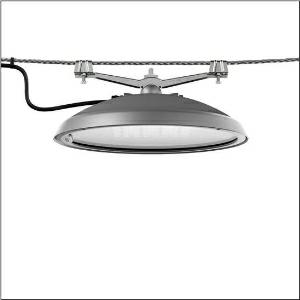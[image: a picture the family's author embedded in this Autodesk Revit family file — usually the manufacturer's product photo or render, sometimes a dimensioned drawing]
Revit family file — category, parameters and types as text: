
# Revit family: dl_50_iq_mini___st1_0s_5xa248w31f08he_4c20
name_source: partatom
category: Lighting Fixtures
units: mm (PartAtom-declared; Revit-internal decimal feet)

## family parameters
Cut with Voids When Loaded = No
Host = Face
Light Source = No
Part Type = Normal
Room Calculation Point = No
Round Connector Dimension = Use Diameter
Shared = No

## types (1)
- --- (1 x LED, 9400 lm, 68.6 W, 3000K)
    Apparent Load = 69 VA
    CIE Flux Codes = 37 72 97 100 100
    Color Rendering = 70
    Color Temperature = 3000K
    Default Elevation = 1800 mm
    Description = DL 50 iQ mini, catenary luminaire, primary light control with lens, of PMMA, primary optical cover: cover, of toughened safety glass, transparent, light distribution: ST1.0s, light emission: direct distribution, primary light characteristic: symmetric, installation type: suspended mounting, LED, High Power LED, rated luminous flux: 9.400lm, luminous efficacy: 137lm/W, light colour: 730, colour temperature: 3000K, control gear: iQ Street-Remote, control: optimised constant luminous flux control (CLO 2.0), Desk-Remote (wireless, voltage-free reading and setting of iQ features in the workshop via application-optimized NFC function/RFID function), Light-Fading, Smart-Wire, Night-Set, Lumen-Switch, Temp-Guard, Auto-Match, Street-Remote, mains connection: 230..240V, AC, 50/60Hz, start of lifetime: 69W, end of service life: 72W, reduction: 30W, luminaire housing, of diecast aluminium, powder-coated, SITECO metallic grey (DB 702S), diameter: 500mm, height: 115mm, mounting height: 4..12m, protection rating (complete): IP66, insulation class (complete): insulation class II (safety insulation), certification: CE, ENEC, ENEC+, VDE, impact resistance: IK08, permissible operating ambient temperature for outdoor applications: -25..+40°C, standard-compliant lighting for roads and squares, packaging unit: 1 piece

Light Distribution: ST1.0s
    Height = 124 mm  [stored 0.406824 ft]
    Lamp = 1 x LED
    Lamp Light Flux = 9400 lm
    Lamp Power = 68.6 W
    Lamp count = 1
    Length = 500 mm
    Luminous efficacy = 137 lm/W
    Manufacturer = Siteco
    ModVariant = No
    Model = 5XA248W31F08HE
    Number of Poles = 1
    OnlyDefault = Yes
    Power Factor = 1
    Product Name = DL 50 iQ mini | ST1.0s
    Product group = catenary luminaire
    ProductGroupID = 6300
    Protection Class = Protection class II
    Protection Degree = IP 66
    RLX_Detail_Level = 1
    RLX_Emergency_Light_Flux = 0 lm
    RLX_Emergency_Type = 0
    RLX_Emergency_Type_DB = No
    RlxData = <blob elided: 123877 chars, md5=08c67c2c>
    Socket = socket
    Standby Power = 0 W
    System Light Flux = 9400 lm
    System Power = 69 W
    Type Comments = factory setting: luminous flux: 100 % | dim-lin: 254 | 693 mA
    Type Image = l_1242791.jpg
    URL = http://relux.com
    VarID = @adj_140135
    Voltage = 0 V
    Weight = 0.00 kg
    Width = 0 mm  [stored 0 ft]

note: [stored X ft] marks values corroborated as IEEE doubles in the binary element streams (Revit-internal decimal feet)

## geometry (parser evidence)
native form markers: Blend x4, Sweep x12
no freeform markers — native parametric forms only
